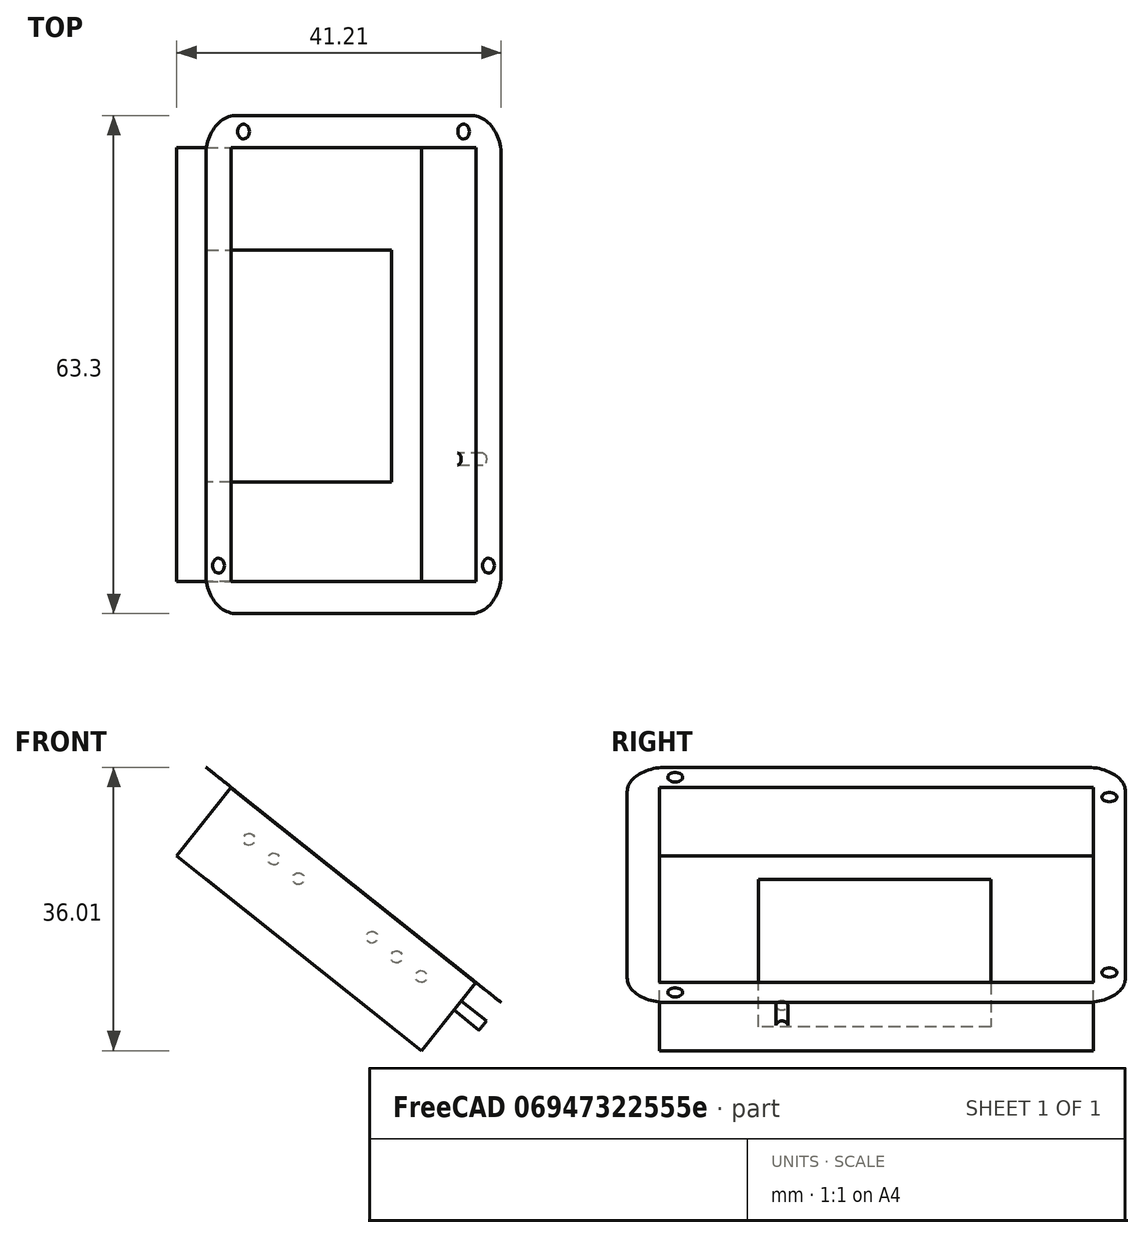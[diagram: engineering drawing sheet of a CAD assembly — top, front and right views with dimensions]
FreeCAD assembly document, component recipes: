
FREECAD ASSEMBLY — COMPONENT RECIPES ("sensor-assembly3")

This assembly document has 2 components, labeled P0..P1 below (a component is one placed body or linked part). 0 of them carry a construction recipe — the FreeCAD feature program that regenerates the part from scratch, quoted from this document or its linked companion documents; the rest are supplied as boundary geometry only. No exploded tour is included for this assembly.
COMPONENT P0 — geometry summary ("enclosure"; no construction recipe available for this part):
  bounding box: 63.3 x 44.2 x 38.5 mm
  tessellated surface: 27,516 triangles
  volume: 10036 mm^3 (9% of its bounding box)
COMPONENT P1 — geometry summary ("electronics"; no construction recipe available for this part):
  bounding box: 55.1 x 37.9 x 33.4 mm
  tessellated surface: 12 triangles
  volume: 24092 mm^3 (35% of its bounding box)
  symmetry: 2-fold rotationally symmetric about the y axis; mirror-symmetric across its y mid-plane
PROVENANCE & LICENSES
A FreeCAD (.FCStd) document from a public repository crawl; recipes are the document's own serialized feature recipes (and, for linked parts, companion documents' recipes).
License: agpl-3.0.
